# Revit family: Buzzispace - BuzziLoose 1
name_source: partatom
category: Furniture
units: mm (PartAtom-declared; Revit-internal decimal feet)

## family parameters
Always vertical = Yes
Cut with Voids When Loaded = No
Host = Ceiling
Room Calculation Point = No
Shared = No

## types (10) — shared parameters
Manufacturer = Buzzispace
Model = BuzziLoose

## per-type parameters (varying)
| type | 3D | 3D L | 3D M | 3D S | 3D XL | 3D XS | Cable Location | Flat | Height | Width |
| Flat - XS | No | No | No | No | No | No | 40 cm | Yes | 60 cm | 80 cm |
| Flat - S | No | No | No | No | No | No | 80 cm | Yes | 80 cm | 120 cm |
| Flat - M | No | No | No | No | No | No | 120 cm | Yes | 80 cm | 160 cm |
| Flat - L | No | No | No | No | No | No | 140 cm | Yes | 100 cm | 180 cm |
| Flat - XL | No | No | No | No | No | No | 160 cm | Yes | 120 cm | 200 cm |
| 3D - XS | Yes | No | No | No | No | Yes | 40 cm | No | 60 cm | 80 cm |
| 3D - S | Yes | No | No | Yes | No | No | 80 cm | No | 80 cm | 120 cm |
| 3D - M | Yes | No | Yes | No | No | No | 120 cm | No | 80 cm | 160 cm |
| 3D - L | Yes | Yes | No | No | No | No | 140 cm | No | 100 cm | 180 cm |
| 3D - XL | Yes | No | No | No | Yes | No | 160 cm | No | 120 cm | 200 cm |

## geometry (parser evidence)
native form markers: Sweep x4
no freeform markers — native parametric forms only
